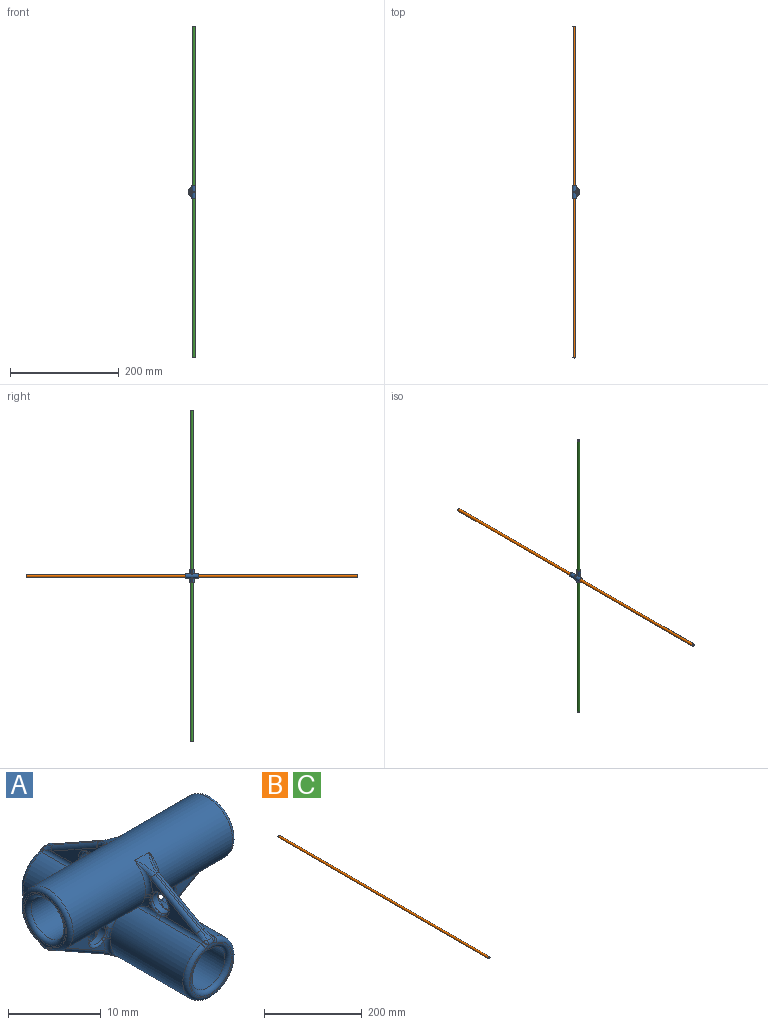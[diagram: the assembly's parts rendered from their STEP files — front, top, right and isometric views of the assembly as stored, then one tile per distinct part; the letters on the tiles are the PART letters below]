
ASSEMBLY  parts=3 mates=1
PART A: 180 faces, bbox 25.4x25.4x15.2 mm
  f0: plane 6.99x3.95mm, normal (0,-1,0), area 6.9mm2, adj f56,f59,f94,f144
  f1: plane 0.85x0.55mm, normal (0,1,0), area 0.2mm2, adj f62,f63,f139
  f2: plane 0.85x0.55mm, normal (0,-1,0), area 0.2mm2, adj f66,f67,f133
  f3: plane 6.99x3.95mm, normal (0,1,0), area 6.9mm2, adj f68,f71,f85,f126
  f4: plane 6.98x3.93mm, normal (-1,0,0), area 6.4mm2, adj f50,f55,f103,f153
  f5: plane 6.98x3.93mm, normal (1,0,0), area 6.4mm2, adj f44,f49,f109,f159
  f6: plane 6.98x3.93mm, normal (-1,0,0), area 6.4mm2, adj f38,f43,f112,f167
  f7: plane 6.98x3.93mm, normal (1,0,0), area 6.4mm2, adj f32,f37,f118,f177
  f8: cylinder r=3.81mm len=24.38mm, axis (0,1,0), area 487.7mm2, adj f12,f18,f22,f34,f35,f36,f37,f40
  f9: cylinder r=2.6mm len=24.38mm, axis (0,1,0), area 398.9mm2, adj f122,f123
  f10: plane 6.82x6.6mm, normal (0,-1,0), area 4.1mm2, adj f78,f79,f80,f106,f123
  f11: plane 6.82x6.6mm, normal (0,1,0), area 4.1mm2, adj f81,f82,f83,f115,f122
  f12: cylinder r=3.81mm len=24.38mm, axis (-1,0,0), area 489.1mm2, adj f8,f24,f28,f32,f33,f34,f38,f39
  f13: cylinder r=2.6mm len=24.38mm, axis (-1,0,0), area 398.9mm2, adj f120,f121
  f14: plane 6.82x6.6mm, normal (1,0,0), area 4.1mm2, adj f72,f73,f74,f88,f121
  f15: plane 6.82x6.6mm, normal (-1,0,0), area 4.1mm2, adj f75,f76,f77,f97,f120
  f16: plane 6.99x3.95mm, normal (0,-1,0), area 6.9mm2, adj f64,f67,f91,f130
  f17: plane 0.85x0.55mm, normal (0,1,0), area 0.2mm2, adj f70,f71,f125
  f18: plane 10.61x6.01mm, normal (0.49,0,-0.87), area 5.4mm2, adj f8,f84,f85,f86,f88,f90,f91,f92
  f19: cylinder r=1.27mm len=2.54mm, axis (0,1,0), area 6.3mm2, adj f124,f125,f126,f127,f128,f129,f130,f131
  f20: plane 0.85x0.55mm, normal (0,-1,0), area 0.2mm2, adj f56,f57,f143
  f21: plane 6.99x3.95mm, normal (0,1,0), area 6.9mm2, adj f60,f63,f100,f136
  f22: plane 10.61x6.01mm, normal (-0.49,0,-0.87), area 5.4mm2, adj f8,f93,f94,f95,f97,f99,f100,f101
  f23: cylinder r=1.27mm len=2.54mm, axis (0,1,0), area 6.3mm2, adj f136,f137,f138,f139,f140,f141,f142,f143
  f24: plane 10.35x5.85mm, normal (0,0.49,0.87), area 4.8mm2, adj f12,f111,f112,f113,f115,f117,f118,f119
  f25: cylinder r=1.27mm len=2.54mm, axis (-1,0,0), area 6.2mm2, adj f164,f165,f166,f167,f168,f169,f170,f171
  f26: plane 0.99x0.78mm, normal (1,0,0), area 0.3mm2, adj f34,f35,f174
  f27: plane 0.99x0.78mm, normal (-1,0,0), area 0.3mm2, adj f40,f41,f168
  f28: plane 10.35x5.85mm, normal (0,-0.49,0.87), area 4.8mm2, adj f12,f102,f103,f104,f106,f108,f109,f110
  f29: cylinder r=1.27mm len=2.54mm, axis (-1,0,0), area 6.2mm2, adj f148,f149,f150,f151,f152,f153,f154,f155
  f30: plane 0.99x0.78mm, normal (1,0,0), area 0.3mm2, adj f46,f47,f160
  f31: plane 0.99x0.78mm, normal (-1,0,0), area 0.3mm2, adj f52,f53,f150
  f32: torus R=4.32mm, axis (1,0,0), area 2.6mm2, adj f7,f12,f33,f119,f179
  f33: bspline ~0.69x0.65mm, area 0.2mm2, adj f12,f32,f34,f178
  f34: torus R=4.32mm, axis (1,0,0), area 1.5mm2, adj f8,f12,f26,f33,f35,f176
  f35: cylinder r=0.51mm len=2.72mm, axis (0,1,0), area 1.4mm2, adj f8,f26,f34,f36,f172
  f36: bspline ~0.88x0.55mm, area 0.2mm2, adj f8,f35,f37,f173
  f37: cylinder r=0.51mm len=6.5mm, axis (0,1,0), area 4mm2, adj f7,f8,f36,f81,f117,f175
  f38: torus R=4.32mm, axis (1,0,0), area 2.6mm2, adj f6,f12,f39,f111,f169
  f39: bspline ~0.69x0.65mm, area 0.2mm2, adj f12,f38,f40,f171
  f40: torus R=4.32mm, axis (1,0,0), area 1.5mm2, adj f8,f12,f27,f39,f41,f170
  f41: cylinder r=0.51mm len=2.72mm, axis (0,1,0), area 1.4mm2, adj f8,f27,f40,f42,f166
  f42: bspline ~0.83x0.55mm, area 0.2mm2, adj f8,f41,f43,f164
  f43: cylinder r=0.51mm len=6.5mm, axis (0,1,0), area 4mm2, adj f6,f8,f42,f83,f113,f165
  f44: cylinder r=0.51mm len=6.5mm, axis (0,1,0), area 4mm2, adj f5,f8,f45,f78,f108,f157
  f45: bspline ~0.83x0.55mm, area 0.2mm2, adj f8,f44,f46,f156
  f46: cylinder r=0.51mm len=2.72mm, axis (0,1,0), area 1.4mm2, adj f8,f30,f45,f47,f158
  f47: torus R=4.32mm, axis (1,0,0), area 1.5mm2, adj f8,f12,f30,f46,f48,f162
  f48: bspline ~0.69x0.65mm, area 0.2mm2, adj f12,f47,f49,f163
  f49: torus R=4.32mm, axis (1,0,0), area 2.6mm2, adj f5,f12,f48,f110,f161
  f50: cylinder r=0.51mm len=6.5mm, axis (0,1,0), area 4mm2, adj f4,f8,f51,f80,f104,f151
  f51: bspline ~0.88x0.55mm, area 0.2mm2, adj f8,f50,f52,f149
  f52: cylinder r=0.51mm len=2.72mm, axis (0,1,0), area 1.4mm2, adj f8,f31,f51,f53,f148
  f53: torus R=4.32mm, axis (1,0,0), area 1.5mm2, adj f8,f12,f31,f52,f54,f152
  f54: bspline ~0.69x0.65mm, area 0.2mm2, adj f12,f53,f55,f154
  f55: torus R=4.32mm, axis (1,0,0), area 2.6mm2, adj f4,f12,f54,f102,f155
  f56: cylinder r=0.51mm len=9.73mm, axis (-1,0,0), area 5.7mm2, adj f0,f12,f20,f57,f75,f95,f142
  f57: torus R=4.32mm, axis (0,-1,0), area 1.2mm2, adj f8,f12,f20,f56,f58,f145
  f58: bspline ~1.72x0.97mm, area 0.6mm2, adj f8,f57,f59,f147
  f59: torus R=4.32mm, axis (0,-1,0), area 2.4mm2, adj f0,f8,f58,f93,f146
  f60: torus R=4.32mm, axis (0,-1,0), area 2.4mm2, adj f8,f21,f61,f101,f138
  f61: bspline ~1.72x0.97mm, area 0.6mm2, adj f8,f60,f62,f140
  f62: torus R=4.32mm, axis (0,-1,0), area 1.2mm2, adj f1,f8,f12,f61,f63,f141
  f63: cylinder r=0.51mm len=9.73mm, axis (-1,0,0), area 5.7mm2, adj f1,f12,f21,f62,f77,f99,f137
  f64: torus R=4.32mm, axis (0,-1,0), area 2.4mm2, adj f8,f16,f65,f92,f132
  f65: bspline ~1.72x0.97mm, area 0.6mm2, adj f8,f64,f66,f134
  f66: torus R=4.32mm, axis (0,-1,0), area 1.2mm2, adj f2,f8,f12,f65,f67,f135
  f67: cylinder r=0.51mm len=9.73mm, axis (-1,0,0), area 5.7mm2, adj f2,f12,f16,f66,f72,f90,f131
  f68: torus R=4.32mm, axis (0,-1,0), area 2.4mm2, adj f3,f8,f69,f84,f128
  f69: bspline ~1.72x0.97mm, area 0.6mm2, adj f8,f68,f70,f129
  f70: torus R=4.32mm, axis (0,-1,0), area 1.2mm2, adj f8,f12,f17,f69,f71,f127
  f71: cylinder r=0.51mm len=9.73mm, axis (-1,0,0), area 5.7mm2, adj f3,f12,f17,f70,f74,f86,f124
  f72: torus R=1.02mm, axis (1,0,0), area 0.3mm2, adj f14,f67,f73,f89
  f73: torus R=3.3mm, axis (1,0,0), area 16.6mm2, adj f12,f14,f72,f74
  f74: torus R=1.02mm, axis (1,0,0), area 0.3mm2, adj f14,f71,f73,f87
  f75: torus R=1.02mm, axis (1,0,0), area 0.3mm2, adj f15,f56,f76,f96
  f76: torus R=3.3mm, axis (1,0,0), area 16.6mm2, adj f12,f15,f75,f77
  f77: torus R=1.02mm, axis (1,0,0), area 0.3mm2, adj f15,f63,f76,f98
  f78: torus R=1.02mm, axis (0,-1,0), area 0.3mm2, adj f10,f44,f79,f107
  f79: torus R=3.3mm, axis (0,-1,0), area 16.6mm2, adj f8,f10,f78,f80
  f80: torus R=1.02mm, axis (0,-1,0), area 0.3mm2, adj f10,f50,f79,f105
  f81: torus R=1.02mm, axis (0,-1,0), area 0.3mm2, adj f11,f37,f82,f116
  f82: torus R=3.3mm, axis (0,-1,0), area 16.6mm2, adj f8,f11,f81,f83
  f83: torus R=1.02mm, axis (0,-1,0), area 0.3mm2, adj f11,f43,f82,f114
  f84: bspline ~2.42x1.81mm, area 0.8mm2, adj f18,f68,f85
  f85: cylinder r=0.51mm len=7.24mm, axis (0.87,0,0.49), area 6.4mm2, adj f3,f18,f84,f86
  f86: bspline ~1.4x0.77mm, area 0.8mm2, adj f18,f71,f85,f87
  f87: sphere r=0.51mm, area 0.2mm2, adj f74,f86,f88
  f88: cylinder r=0.51mm len=0.73mm, axis (0,1,0), area 0.4mm2, adj f14,f18,f87,f89
  f89: sphere r=0.51mm, area 0.2mm2, adj f72,f88,f90
  f90: bspline ~1.4x0.77mm, area 0.8mm2, adj f18,f67,f89,f91
  f91: cylinder r=0.51mm len=7.24mm, axis (-0.87,0,-0.49), area 6.4mm2, adj f16,f18,f90,f92
  f92: bspline ~2.53x1.88mm, area 0.8mm2, adj f18,f64,f91
  f93: bspline ~2.42x1.81mm, area 0.8mm2, adj f22,f59,f94
  f94: cylinder r=0.51mm len=7.24mm, axis (0.87,0,-0.49), area 6.4mm2, adj f0,f22,f93,f95
  f95: bspline ~1.4x0.77mm, area 0.8mm2, adj f22,f56,f94,f96
  f96: sphere r=0.51mm, area 0.2mm2, adj f75,f95,f97
  f97: cylinder r=0.51mm len=0.73mm, axis (0,-1,0), area 0.4mm2, adj f15,f22,f96,f98
  f98: sphere r=0.51mm, area 0.2mm2, adj f77,f97,f99
  f99: bspline ~1.4x0.77mm, area 0.8mm2, adj f22,f63,f98,f100
  f100: cylinder r=0.51mm len=7.24mm, axis (-0.87,0,0.49), area 6.4mm2, adj f21,f22,f99,f101
  f101: bspline ~2.42x1.81mm, area 0.8mm2, adj f22,f60,f100
  f102: bspline ~2.28x1.74mm, area 1.1mm2, adj f12,f28,f55,f103
  f103: cylinder r=0.51mm len=7.23mm, axis (0,0.87,0.49), area 6.4mm2, adj f4,f28,f102,f104
  f104: bspline ~1.41x0.77mm, area 0.8mm2, adj f28,f50,f103,f105
  f105: sphere r=0.51mm, area 0.2mm2, adj f80,f104,f106
  f106: cylinder r=0.51mm len=0.73mm, axis (1,0,0), area 0.4mm2, adj f10,f28,f105,f107
  f107: sphere r=0.51mm, area 0.2mm2, adj f78,f106,f108
  f108: bspline ~1.41x0.77mm, area 0.8mm2, adj f28,f44,f107,f109
  f109: cylinder r=0.51mm len=7.23mm, axis (0,-0.87,-0.49), area 6.4mm2, adj f5,f28,f108,f110
  f110: bspline ~2.28x1.74mm, area 1.1mm2, adj f12,f28,f49,f109
  f111: bspline ~2.28x1.74mm, area 1.1mm2, adj f12,f24,f38,f112
  f112: cylinder r=0.51mm len=7.23mm, axis (0,-0.87,0.49), area 6.4mm2, adj f6,f24,f111,f113
  f113: bspline ~1.41x0.77mm, area 0.8mm2, adj f24,f43,f112,f114
  f114: sphere r=0.51mm, area 0.2mm2, adj f83,f113,f115
  f115: cylinder r=0.51mm len=0.73mm, axis (-1,0,0), area 0.4mm2, adj f11,f24,f114,f116
  f116: sphere r=0.51mm, area 0.2mm2, adj f81,f115,f117
  f117: bspline ~1.41x0.77mm, area 0.8mm2, adj f24,f37,f116,f118
  f118: cylinder r=0.51mm len=7.23mm, axis (0,0.87,-0.49), area 6.4mm2, adj f7,f24,f117,f119
  f119: bspline ~2.28x1.74mm, area 1.1mm2, adj f12,f24,f32,f118
  f120: torus R=3.11mm, axis (1,0,0), area 14mm2, adj f13,f15
  f121: torus R=3.11mm, axis (1,0,0), area 14mm2, adj f13,f14
  f122: torus R=3.11mm, axis (0,-1,0), area 14mm2, adj f9,f11
  f123: torus R=3.11mm, axis (0,-1,0), area 14mm2, adj f9,f10
  f124: bspline ~1.88x0.5mm, area 0.5mm2, adj f19,f71,f125,f126
  f125: torus R=1.52mm, axis (0,-1,0), area 0.3mm2, adj f17,f19,f124,f127
  f126: torus R=1.52mm, axis (0,-1,0), area 1.7mm2, adj f3,f19,f124,f128
  f127: bspline ~0.68x0.36mm, area 0.1mm2, adj f19,f70,f125,f129
  f128: bspline ~0.62x0.53mm, area 0.1mm2, adj f19,f68,f126,f129
  f129: bspline ~1.72x0.62mm, area 0.3mm2, adj f19,f69,f127,f128
  f130: torus R=1.52mm, axis (0,-1,0), area 1.7mm2, adj f16,f19,f131,f132
  f131: bspline ~2.03x0.5mm, area 0.5mm2, adj f19,f67,f130,f133
  f132: bspline ~0.62x0.53mm, area 0.1mm2, adj f19,f64,f130,f134
  f133: torus R=1.52mm, axis (0,-1,0), area 0.3mm2, adj f2,f19,f131,f135
  f134: bspline ~1.73x0.62mm, area 0.3mm2, adj f19,f65,f132,f135
  f135: bspline ~0.68x0.36mm, area 0.1mm2, adj f19,f66,f133,f134
  f136: torus R=1.52mm, axis (0,-1,0), area 1.7mm2, adj f21,f23,f137,f138
  f137: bspline ~2.03x0.5mm, area 0.5mm2, adj f23,f63,f136,f139
  f138: bspline ~0.62x0.53mm, area 0.1mm2, adj f23,f60,f136,f140
  f139: torus R=1.52mm, axis (0,-1,0), area 0.3mm2, adj f1,f23,f137,f141
  f140: bspline ~1.73x0.62mm, area 0.3mm2, adj f23,f61,f138,f141
  f141: bspline ~0.68x0.36mm, area 0.1mm2, adj f23,f62,f139,f140
  f142: bspline ~1.88x0.5mm, area 0.5mm2, adj f23,f56,f143,f144
  f143: torus R=1.52mm, axis (0,-1,0), area 0.3mm2, adj f20,f23,f142,f145
  f144: torus R=1.52mm, axis (0,-1,0), area 1.7mm2, adj f0,f23,f142,f146
  f145: bspline ~0.68x0.36mm, area 0.1mm2, adj f23,f57,f143,f147
  f146: bspline ~0.62x0.53mm, area 0.1mm2, adj f23,f59,f144,f147
  f147: bspline ~1.72x0.62mm, area 0.3mm2, adj f23,f58,f145,f146
  f148: bspline ~1x0.43mm, area 0.2mm2, adj f29,f52,f149,f150
  f149: bspline ~0.67x0.25mm, area 0.1mm2, adj f29,f51,f148,f151
  f150: torus R=1.52mm, axis (1,0,0), area 0.3mm2, adj f29,f31,f148,f152
  f151: bspline ~0.93x0.53mm, area 0.2mm2, adj f29,f50,f149,f153
  f152: bspline ~0.82x0.32mm, area 0.2mm2, adj f29,f53,f150,f154
  f153: torus R=1.52mm, axis (1,0,0), area 1.8mm2, adj f4,f29,f151,f155
  f154: bspline ~0.47x0.26mm, area 0.1mm2, adj f29,f54,f152,f155
  f155: bspline ~0.85x0.51mm, area 0.2mm2, adj f29,f55,f153,f154
  f156: bspline ~0.67x0.25mm, area 0.1mm2, adj f29,f45,f157,f158
  f157: bspline ~0.93x0.53mm, area 0.2mm2, adj f29,f44,f156,f159
  f158: bspline ~1x0.43mm, area 0.2mm2, adj f29,f46,f156,f160
  f159: torus R=1.52mm, axis (1,0,0), area 1.8mm2, adj f5,f29,f157,f161
  f160: torus R=1.52mm, axis (1,0,0), area 0.3mm2, adj f29,f30,f158,f162
  f161: bspline ~0.85x0.51mm, area 0.2mm2, adj f29,f49,f159,f163
  f162: bspline ~0.82x0.32mm, area 0.2mm2, adj f29,f47,f160,f163
  f163: bspline ~0.47x0.26mm, area 0.1mm2, adj f29,f48,f161,f162
  f164: bspline ~0.67x0.25mm, area 0.1mm2, adj f25,f42,f165,f166
  f165: bspline ~0.93x0.53mm, area 0.2mm2, adj f25,f43,f164,f167
  f166: bspline ~1x0.43mm, area 0.2mm2, adj f25,f41,f164,f168
  f167: torus R=1.52mm, axis (1,0,0), area 1.8mm2, adj f6,f25,f165,f169
  f168: torus R=1.52mm, axis (1,0,0), area 0.3mm2, adj f25,f27,f166,f170
  f169: bspline ~0.85x0.51mm, area 0.2mm2, adj f25,f38,f167,f171
  f170: bspline ~0.82x0.32mm, area 0.2mm2, adj f25,f40,f168,f171
  f171: bspline ~0.47x0.26mm, area 0.1mm2, adj f25,f39,f169,f170
  f172: bspline ~1x0.43mm, area 0.2mm2, adj f25,f35,f173,f174
  f173: bspline ~0.67x0.25mm, area 0.1mm2, adj f25,f36,f172,f175
  f174: torus R=1.52mm, axis (1,0,0), area 0.3mm2, adj f25,f26,f172,f176
  f175: bspline ~0.93x0.53mm, area 0.2mm2, adj f25,f37,f173,f177
  f176: bspline ~0.82x0.32mm, area 0.2mm2, adj f25,f34,f174,f178
  f177: torus R=1.52mm, axis (1,0,0), area 1.8mm2, adj f7,f25,f175,f179
  f178: bspline ~0.47x0.26mm, area 0.1mm2, adj f25,f33,f176,f179
  f179: bspline ~0.85x0.51mm, area 0.2mm2, adj f25,f32,f177,f178
PART B: 4 faces, bbox 5.1x609.6x5.1 mm
  f0: cylinder r=1.91mm len=609.6mm, axis (0,1,0), area 7296.6mm2, adj f2,f3
  f1: cylinder r=2.54mm len=609.6mm, axis (0,1,0), area 9728.8mm2, adj f2,f3
  f2: plane 5.08x5.08mm, normal (0,-1,0), area 8.9mm2, adj f0,f1
  f3: plane 5.08x5.08mm, normal (0,1,0), area 8.9mm2, adj f0,f1
PART C: same geometry as B
PLACE A rot(axis=(0.58,-0.58,-0.58),120deg) t=(18.87,-3.91,45.75)mm
PLACE B t=(12.26,300.89,45.75)mm
PLACE C rot(axis=(0.58,-0.58,-0.58),120deg) t=(18.87,-3.91,350.55)mm
MATE fastened A.f12 <-> B.f0  axis (0,1,0) through (12.26,-3.91,45.75)mm
